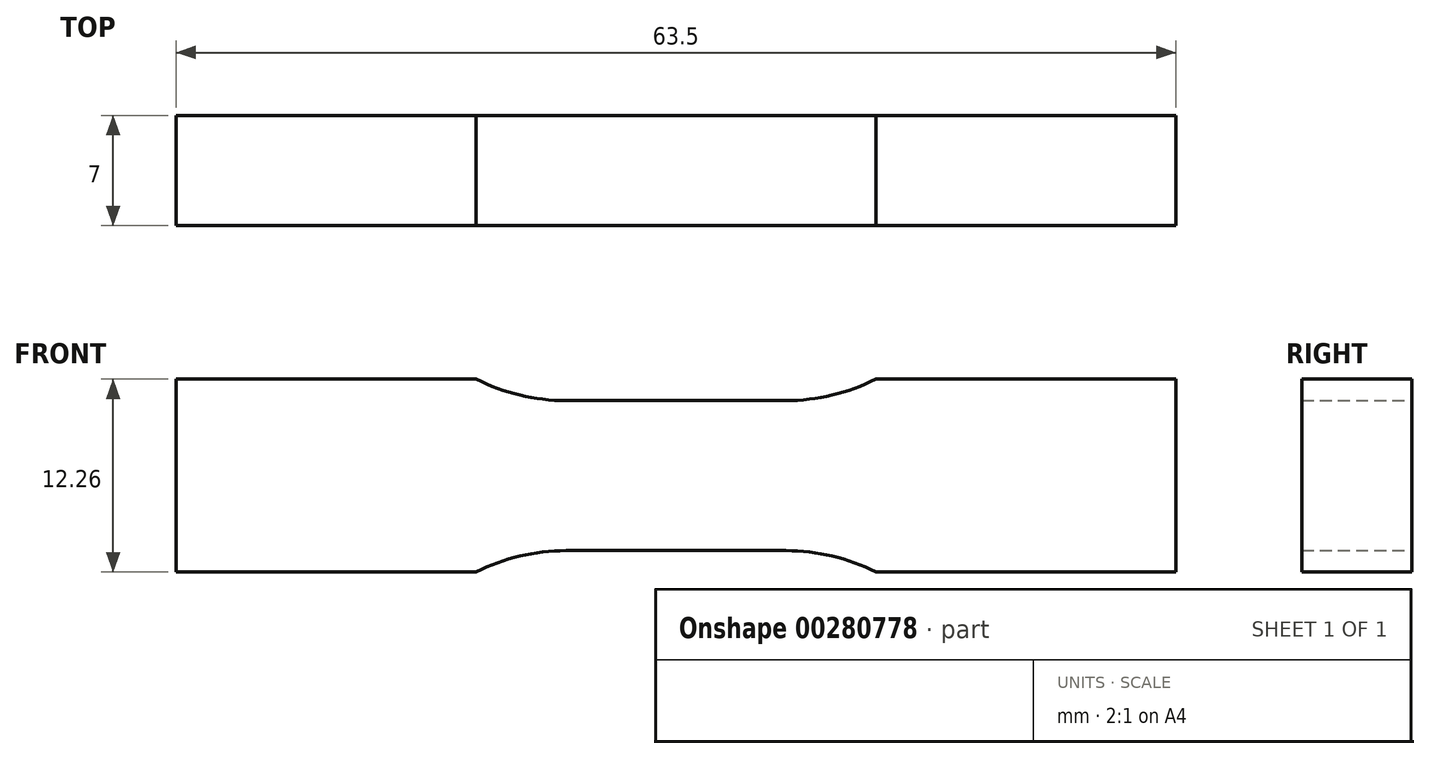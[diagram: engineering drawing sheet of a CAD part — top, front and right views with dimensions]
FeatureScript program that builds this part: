
annotation { "Feature Type Name" : "Feature", "Feature Type Description" : "" }
export const myFeature = defineFeature(function(context is Context, id is Id, definition is map)
    precondition{}
    {
        {
            var Q0;
            Q0=qCreatedBy(makeId("Front.planeOp"),FACE);
            var sketch = newSketch(context, id + "F0", { "sketchPlane" : qUnion([Q0])});
            skLineSegment(sketch, "E0", {"start": v(0, 4.77) * mm, "end": v(6.98, 4.77) * mm});
            skArc(sketch, "E1", {"start": v(6.98, 4.76) * mm, "mid": v(9.92, 5.1) * mm, "end": v(12.7, 6.13) * mm});
            skLineSegment(sketch, "E2", {"start": v(12.7, 6.13) * mm, "end": v(31.75, 6.13) * mm});
            skLineSegment(sketch, "E3.MirrorCS", {"start": v(12.7, -6.13) * mm, "end": v(31.75, -6.13) * mm});
            skLineSegment(sketch, "E4.MirrorCS", {"start": v(0, -4.76) * mm, "end": v(6.98, -4.76) * mm});
            skArc(sketch, "E5.MirrorCS", {"start": v(6.98, -4.76) * mm, "mid": v(9.92, -5.1) * mm, "end": v(12.7, -6.13) * mm});
            skLineSegment(sketch, "E6.MirrorCS", {"start": v(0, -4.77) * mm, "end": v(6.98, -4.77) * mm});
            skLineSegment(sketch, "E7.MirrorCS", {"start": v(0, -4.76) * mm, "end": v(-6.98, -4.76) * mm});
            skArc(sketch, "E8.MirrorCS", {"start": v(-6.98, 4.77) * mm, "mid": v(-9.92, 5.1) * mm, "end": v(-12.7, 6.13) * mm});
            skLineSegment(sketch, "E9.MirrorCS", {"start": v(-12.7, 6.13) * mm, "end": v(-31.75, 6.13) * mm});
            skLineSegment(sketch, "E10.MirrorCS", {"start": v(-12.7, -6.13) * mm, "end": v(-31.75, -6.13) * mm});
            skLineSegment(sketch, "E11.MirrorCS", {"start": v(0, 4.77) * mm, "end": v(-6.98, 4.77) * mm});
            skArc(sketch, "E12.MirrorCS", {"start": v(-6.98, -4.76) * mm, "mid": v(-9.92, -5.1) * mm, "end": v(-12.7, -6.13) * mm});
            skLineSegment(sketch, "E13", {"start": v(-31.75, -6.13) * mm, "end": v(-31.75, 6.13) * mm});
            skLineSegment(sketch, "E14", {"start": v(31.75, 6.13) * mm, "end": v(31.75, -6.13) * mm});
            skSolve(sketch);
        }
        {
            var Q0;
            Q0 = qSketchRegion(id + "F0", true);
            extrude(context, id + "F1", {"entities" : qUnion([Q0]), "endBound" : BoundingType.SYMMETRIC, "depth" : 7 * mm});
        }
    });
